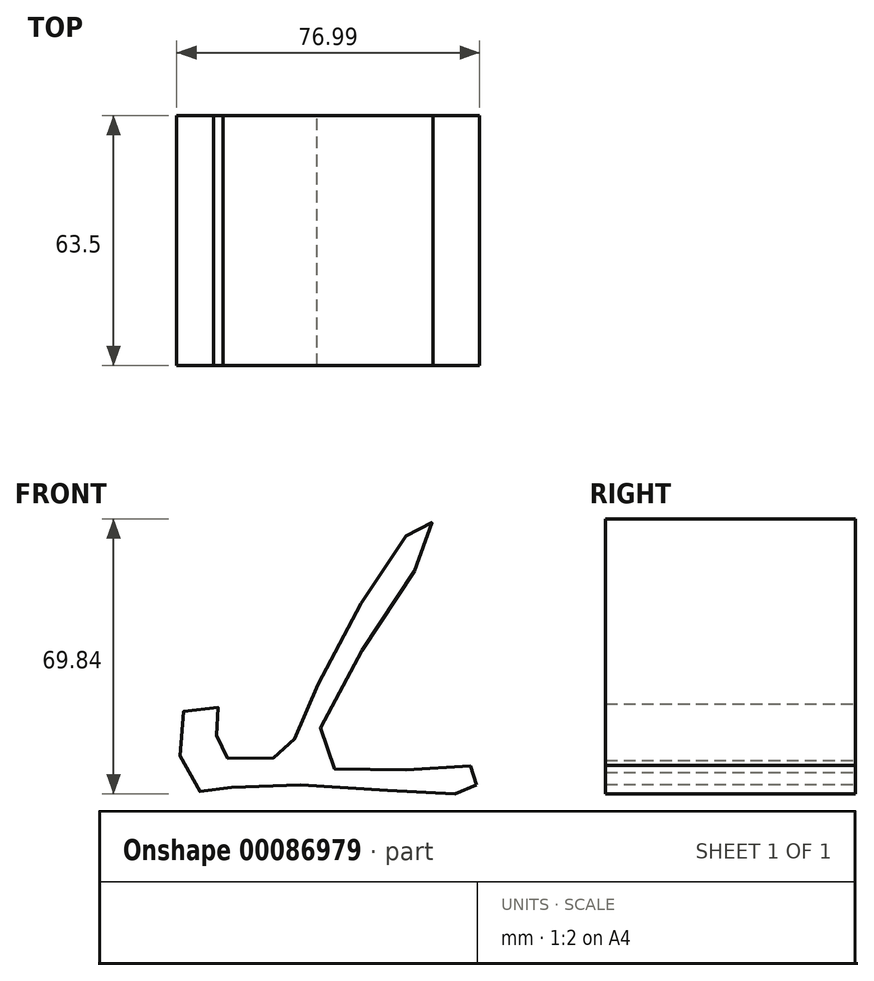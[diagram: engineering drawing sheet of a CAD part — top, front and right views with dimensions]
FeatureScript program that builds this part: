
annotation { "Feature Type Name" : "Feature", "Feature Type Description" : "" }
export const myFeature = defineFeature(function(context is Context, id is Id, definition is map)
    precondition{}
    {
        {
            var Q0;
            Q0=qCreatedBy(makeId("Front.planeOp"),FACE);
            var sketch = newSketch(context, id + "F0", { "sketchPlane" : qUnion([Q0])});
            skFitSpline(sketch, "E0", {"points": [v(33.05, -22.65) * mm, v(32.67, -18.18) * mm, v(-6.61, -16.24) * mm, v(21.39, 39.96) * mm, v(19.66, 44.78) * mm, v(-11.28, -5.93) * mm, v(-17.55, -15.42) * mm, v(-33.61, -13.72) * mm, v(-31.5, -4.2) * mm, v(-41.64, -4.2) * mm, v(-38.26, -23.52) * mm, v(-27.7, -23) * mm, v(28.96, -24.83) * mm, v(33.05, -22.65) * mm]});
            skSolve(sketch);
        }
        {
            var Q0;
            Q0=makeQuery(id+"F0.imprint","IMPRINT",FACE,{"disambiguationData":[TD([[makeQuery(id+"F0.imprint","IMPRINT",EDGE,{"derivedFrom":sQuery(id+"F0.wireOp",EDGE,"E0")}),1.0]])]});
            extrude(context, id + "F1", {"entities" : qUnion([Q0]), "depth" : 63.5 * mm});
        }
    });
